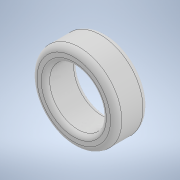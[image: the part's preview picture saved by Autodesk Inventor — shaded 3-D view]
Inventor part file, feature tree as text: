
AUTODESK INVENTOR PART (.ipt)
format: ipt  version: 2021 (Build 250183000, 183)  size: 156,672 bytes
history: native  units: in
note: dims shown in document units (in); Inventor stores cm internally (conversion verified against a paired STEP export)
features: fillet x2, extrude x1, sketch x1
ambient origin geometry x8: Origin, YZ Plane, XZ Plane, XY Plane, X Axis, Y Axis, Z Axis, Center Point
bodies: Solid1 (feature_tree)
feature tree (4):
  extrude  "Extrusion1"  Depth=0.0236in
  fillet  "Fillet2"  Radius=0.1811in
  fillet  "Fillet3"  Radius=0.0315in
  sketch  "Sketch1"  dims[d0=0.4724in d1=0.315in d2=0.1811in d3=0.0in d5=0.0315in d6=0.0236in]
